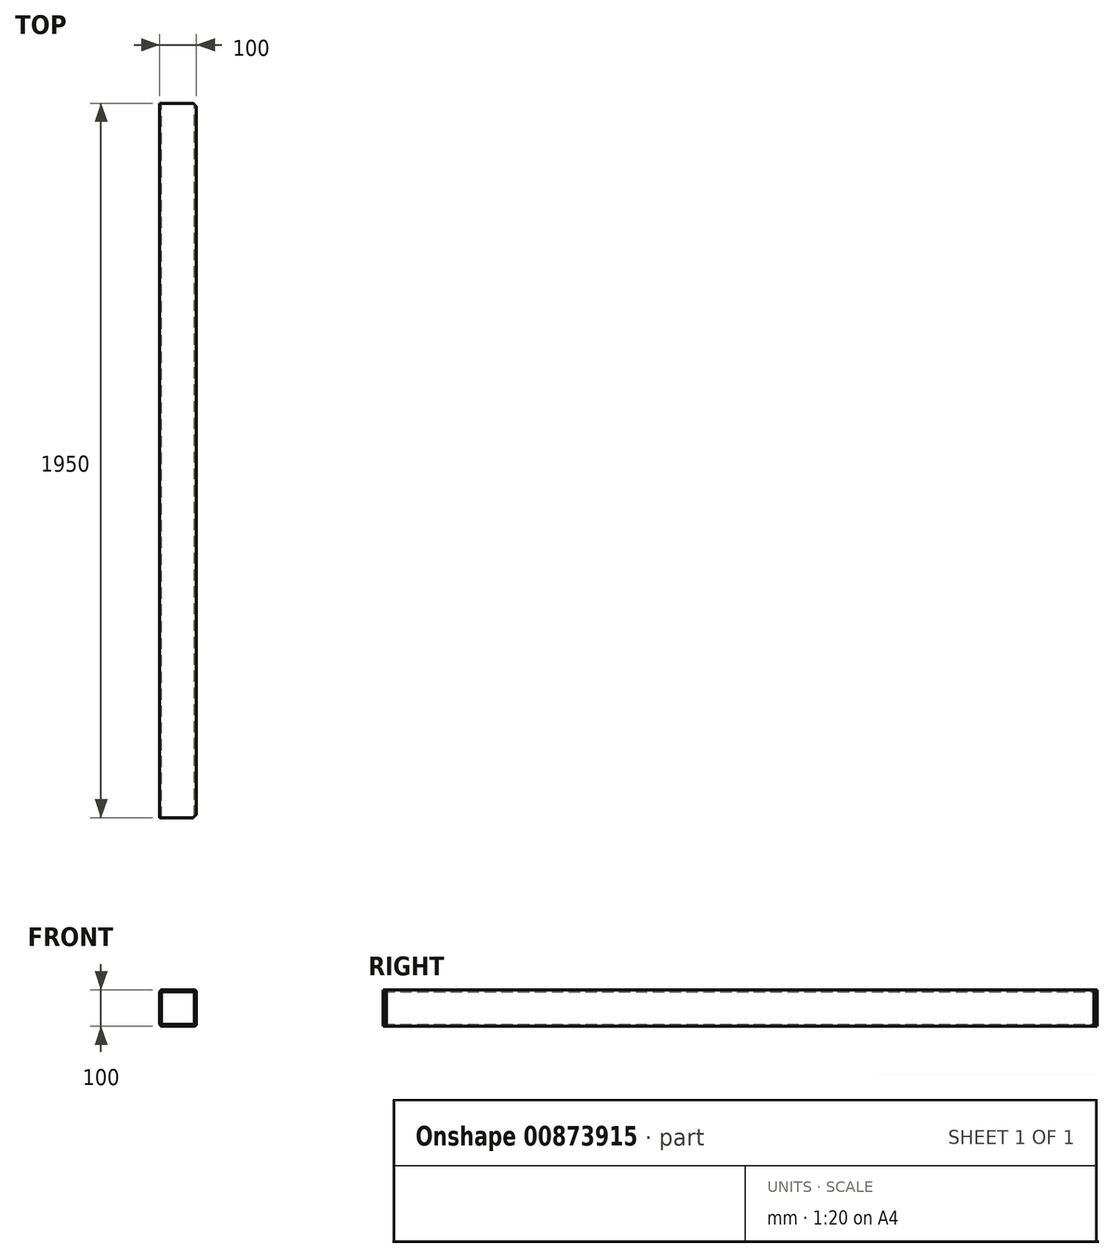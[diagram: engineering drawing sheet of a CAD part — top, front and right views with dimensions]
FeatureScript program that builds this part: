
annotation { "Feature Type Name" : "Feature", "Feature Type Description" : "" }
export const myFeature = defineFeature(function(context is Context, id is Id, definition is map)
    precondition{}
    {
        {
            var Q0;
            Q0=qCreatedBy(makeId("Front.planeOp"),FACE);
            var sketch = newSketch(context, id + "F0", { "sketchPlane" : qUnion([Q0])});
            skLineSegment(sketch, "E0.bottom", {"start": v(43, 50) * mm, "end": v(-43, 50) * mm});
            skLineSegment(sketch, "E0.top", {"start": v(43, -50) * mm, "end": v(-43, -50) * mm});
            skLineSegment(sketch, "E0.left", {"start": v(50, 43) * mm, "end": v(50, -43) * mm});
            skLineSegment(sketch, "E0.right", {"start": v(-50, 43) * mm, "end": v(-50, -43) * mm});
            skPoint(sketch, "E0.middle", {"position": v(0, 0) * mm});
            skPoint(sketch, "E1.visualSharp", {"position": v(-50, 50) * mm});
            skArc(sketch, "E1.filletArc", {"start": v(-43, 50) * mm, "mid": v(-47.95, 47.95) * mm, "end": v(-50, 43) * mm});
            skPoint(sketch, "E2.visualSharp", {"position": v(50, 50) * mm});
            skArc(sketch, "E2.filletArc", {"start": v(50, 43) * mm, "mid": v(47.95, 47.95) * mm, "end": v(43, 50) * mm});
            skPoint(sketch, "E3.visualSharp", {"position": v(-50, -50) * mm});
            skArc(sketch, "E3.filletArc", {"start": v(-50, -43) * mm, "mid": v(-47.95, -47.95) * mm, "end": v(-43, -50) * mm});
            skPoint(sketch, "E4.visualSharp", {"position": v(50, -50) * mm});
            skArc(sketch, "E4.filletArc", {"start": v(43, -50) * mm, "mid": v(47.95, -47.95) * mm, "end": v(50, -43) * mm});
            skLineSegment(sketch, "E5.0", {"start": v(43, -45) * mm, "end": v(-43, -45) * mm});
            skArc(sketch, "E5.1", {"start": v(-45, -43) * mm, "mid": v(-44.41, -44.41) * mm, "end": v(-43, -45) * mm});
            skArc(sketch, "E5.2", {"start": v(43, -45) * mm, "mid": v(44.41, -44.41) * mm, "end": v(45, -43) * mm});
            skLineSegment(sketch, "E5.3", {"start": v(-45, 43) * mm, "end": v(-45, -43) * mm});
            skLineSegment(sketch, "E5.4", {"start": v(45, 43) * mm, "end": v(45, -43) * mm});
            skArc(sketch, "E5.5", {"start": v(45, 43) * mm, "mid": v(44.41, 44.41) * mm, "end": v(43, 45) * mm});
            skLineSegment(sketch, "E5.6", {"start": v(43, 45) * mm, "end": v(-43, 45) * mm});
            skArc(sketch, "E5.7", {"start": v(-43, 45) * mm, "mid": v(-44.41, 44.41) * mm, "end": v(-45, 43) * mm});
            skSolve(sketch);
        }
        {
            var Q0;
            Q0=makeQuery(id+"F0.imprint","IMPRINT",FACE,{"disambiguationData":[TD([[makeQuery(id+"F0.imprint","IMPRINT",EDGE,{"derivedFrom":sQuery(id+"F0.wireOp",EDGE,"E0.bottom")}),1.0]])]});
            extrude(context, id + "F1", {"entities" : qUnion([Q0]), "depth" : 1950 * mm, "offsetDistance" : 25 * mm, "symmetric" : true});
        }
        {
            var Q0;
            Q0=makeQuery(id+"F1.opExtrude","SWEPT_FACE",FACE,{"disambiguationData":[OSD([sQuery(id+"F0.wireOp",EDGE,"E0.bottom")])]});
            var sketch = newSketch(context, id + "F2", { "sketchPlane" : qUnion([Q0])});
            skLineSegment(sketch, "E6.bottom", {"start": v(-50, -1075) * mm, "end": v(50, -1075) * mm, "construction": true});
            skLineSegment(sketch, "E6.top", {"start": v(-50, -975) * mm, "end": v(50, -975) * mm, "construction": true});
            skLineSegment(sketch, "E6.left", {"start": v(-50, -1075) * mm, "end": v(-50, -975) * mm, "construction": true});
            skLineSegment(sketch, "E6.right", {"start": v(50, -1075) * mm, "end": v(50, -975) * mm, "construction": true});
            skLineSegment(sketch, "E7", {"start": v(0, -975) * mm, "end": v(0, 975) * mm, "construction": true});
            skLineSegment(sketch, "E8", {"start": v(-50, -1075) * mm, "end": v(50, -975) * mm, "construction": true});
            skLineSegment(sketch, "E9.bottom", {"start": v(-57.28, -1073.8) * mm, "end": v(55.86, -960.65) * mm});
            skLineSegment(sketch, "E9.top", {"start": v(-48.8, -1082.28) * mm, "end": v(64.35, -969.14) * mm});
            skLineSegment(sketch, "E9.left", {"start": v(-57.28, -1073.8) * mm, "end": v(-48.8, -1082.28) * mm});
            skLineSegment(sketch, "E9.right", {"start": v(55.86, -960.65) * mm, "end": v(64.35, -969.14) * mm});
            skPoint(sketch, "E9.middle", {"position": v(0, -1025) * mm});
            skLineSegment(sketch, "E10.MirrorCS", {"start": v(-57.28, 1073.8) * mm, "end": v(-48.8, 1082.28) * mm});
            skLineSegment(sketch, "E11.MirrorCS", {"start": v(-48.8, 1082.28) * mm, "end": v(64.35, 969.14) * mm});
            skLineSegment(sketch, "E12.MirrorCS", {"start": v(-57.28, 1073.8) * mm, "end": v(55.86, 960.65) * mm});
            skLineSegment(sketch, "E13.MirrorCS", {"start": v(55.86, 960.65) * mm, "end": v(64.35, 969.14) * mm});
            skSolve(sketch);
        }
        {
            var Q0;
            Q0 = qSketchRegion(id + "F2", true);
            extrude(context, id + "F3", {"entities" : qUnion([Q0]), "operationType" : NewBodyOperationType.REMOVE, "endBound" : BoundingType.THROUGH_ALL, "oppositeDirection" : true, "depth" : 25 * mm, "offsetDistance" : 25 * mm});
        }
    });
